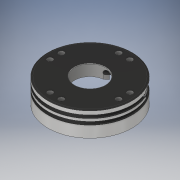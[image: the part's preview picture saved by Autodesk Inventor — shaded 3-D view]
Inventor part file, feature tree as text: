
AUTODESK INVENTOR PART (.ipt)
format: ipt  version: 2019.4 (Build 234330000, 330)  size: 254,976 bytes
history: native  units: mm
features: hole x1
ambient origin geometry x8: Origin, YZ Plane, XZ Plane, XY Plane, X Axis, Y Axis, Z Axis, Center Point
bodies: Solid1 (feature_tree), Body1 (feature_tree)
feature tree (1):
  hole  "Hole Centric Line"  [1 undecoded]
note: 1 required parameter value undecoded (feature->parameter linkage not recoverable at this tier; creation-order binding heuristic only, values carry confidence <= 0.55)
